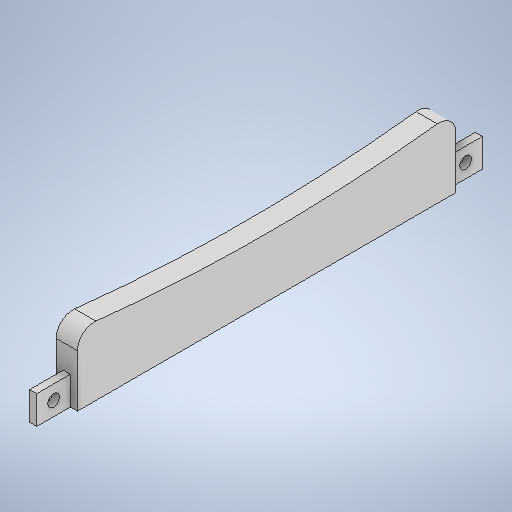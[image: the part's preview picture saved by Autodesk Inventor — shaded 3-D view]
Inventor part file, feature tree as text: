
AUTODESK INVENTOR PART (.ipt)
format: ipt  version: 2025.1 (Build 291241000, 241)  size: 265,216 bytes
history: native  units: in
note: dims shown in document units (in); Inventor stores cm internally (conversion verified against a paired STEP export)
features: extrude x4, sketch x3, fillet x1
ambient origin geometry x8: Origin, YZ Plane, XZ Plane, XY Plane, X Axis, Y Axis, Z Axis, Center Point
bodies: Solid1 (feature_tree)
feature tree (8):
  sketch  "Sketch1"  dims[d6=0.3in d7=0.0in d8=0.75in d9=0.0in]
  extrude  "Extrusion1"  Depth=0.3in TaperAngle=0.0deg
  extrude  "Extrusion2"  Depth=0.5in TaperAngle=0.0deg
  extrude  "Extrusion3"  Depth=0.075in TaperAngle=0.0deg
  extrude  "Extrusion4"  Depth=0.175in
  fillet  "Fillet1"  Radius=4.0in
  sketch  "Sketch2"  dims[d12=0.125in d13=0.5in d14=0.0in]
  sketch  "Sketch3"  dims[d15=0.125in d16=0.5in d17=0.0in d18=0.175in d19=4.0in d20=0.075in d21=0.075in d22=0.075in d23=0.075in d24=0.075in d25=0.075in]
